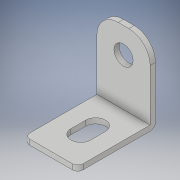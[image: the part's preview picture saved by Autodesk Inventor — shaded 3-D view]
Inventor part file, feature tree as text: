
AUTODESK INVENTOR PART (.ipt)
format: ipt  version: 2018 (Build 220112000, 112)  size: 150,528 bytes
history: native  units: in
note: dims shown in document units (in); Inventor stores cm internally (conversion verified against a paired STEP export)
features: extrude x4, sketch x4, fillet x3
ambient origin geometry x8: Origin, YZ Plane, XZ Plane, XY Plane, X Axis, Y Axis, Z Axis, Center Point
bodies: Solid1 (feature_tree)
feature tree (11):
  extrude  "Extrusion1"  Depth=0.5748in
  extrude  "Extrusion2"  Depth=0.5787in
  fillet  "Fillet1"  Radius=0.0394in
  fillet  "Fillet2"  Radius=0.1575in
  fillet  "Fillet3"  Radius=0.0394in
  extrude  "Extrusion3"  Depth=0.0394in
  extrude  "Extrusion4"  Depth=0.0394in
  sketch  "Sketch1"  dims[d0=0.3937in d1=0.5748in]
  sketch  "Sketch2"  dims[d2=0.0394in d3=0.0in d4=0.5787in d5=0.0394in d6=0.0in d7=0.1575in d8=0.0394in]
  sketch  "Sketch3"  dims[d9=0.0394in d10=0.1969in]
  sketch  "Sketch4"  dims[d11=0.1181in d12=0.1417in d13=0.0394in d14=0.0in d15=0.1457in d16=0.1969in d17=0.1457in d18=0.1457in d19=0.2559in d20=0.124in d21=0.124in d22=0.0394in d23=0.0in]
